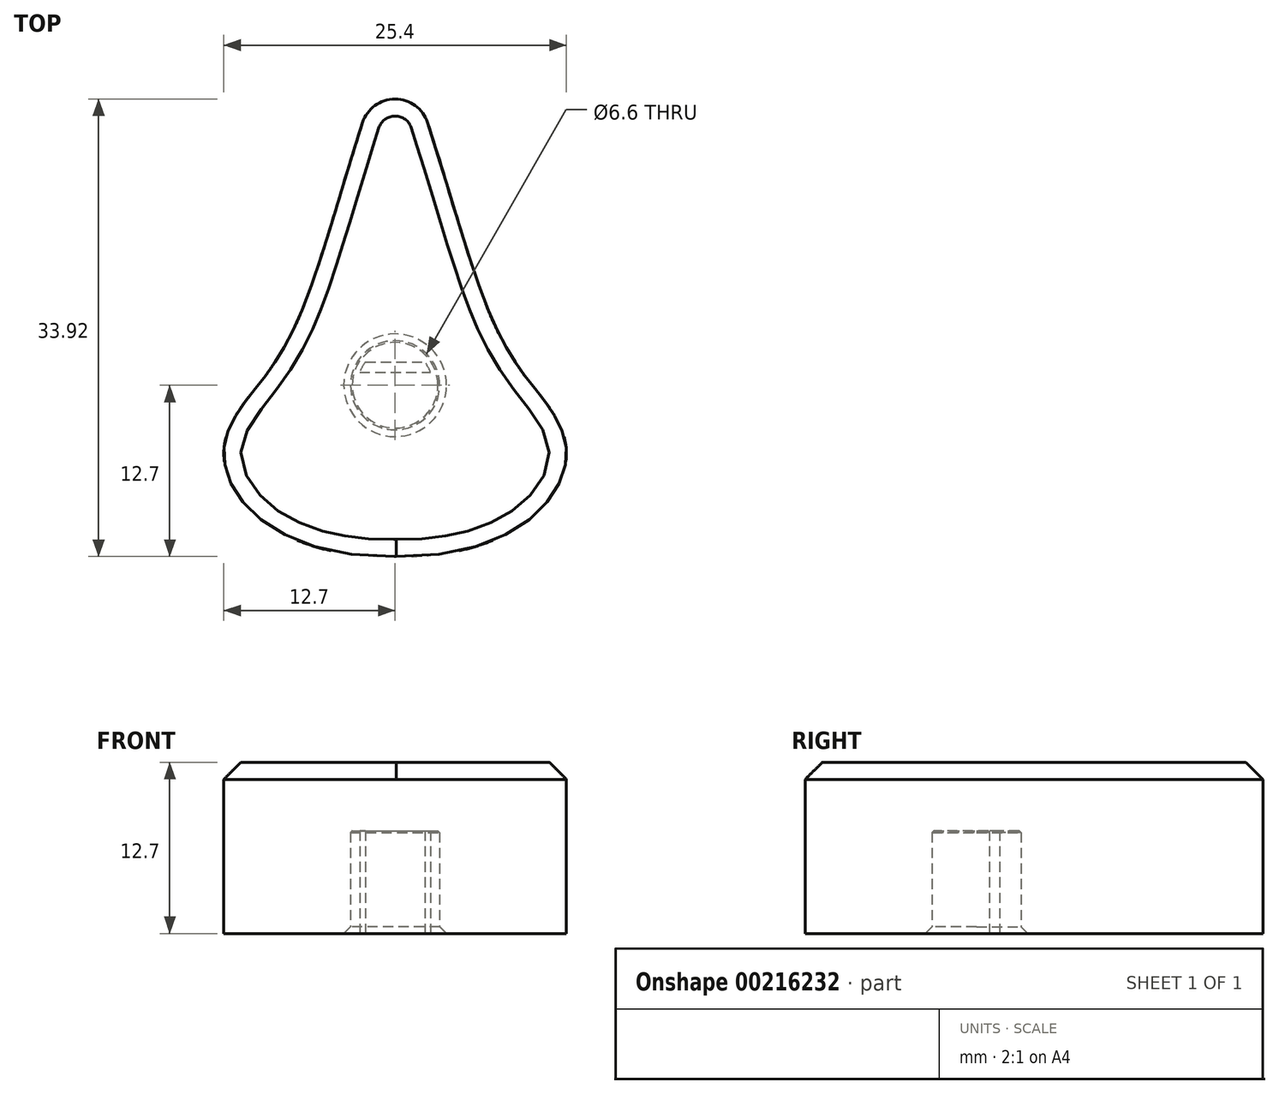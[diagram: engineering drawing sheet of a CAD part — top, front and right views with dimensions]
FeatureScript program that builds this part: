
annotation { "Feature Type Name" : "Feature", "Feature Type Description" : "" }
export const myFeature = defineFeature(function(context is Context, id is Id, definition is map)
    precondition{}
    {
        {
            var Q0;
            Q0=qCreatedBy(makeId("Top.planeOp"),FACE);
            var sketch = newSketch(context, id + "F0", { "sketchPlane" : qUnion([Q0])});
            skLineSegment(sketch, "E0", {"start": v(0, -12.7) * mm, "end": v(0, 25.4) * mm});
            skLineSegment(sketch, "E1", {"start": v(11.05, 11.4) * mm, "end": v(36.75, 22.83) * mm, "construction": true});
            skLineSegment(sketch, "E2", {"start": v(0, 0) * mm, "end": v(39.26, 10.52) * mm, "construction": true});
            skFitSpline(sketch, "E3", {"points": [v(0, -12.7) * mm, v(12.7, -5.22) * mm, v(10.16, 0) * mm, v(6.35, 7) * mm, v(0, 25.4) * mm], "startDerivative": vector(91.13, -1.7) * mm, "endDerivative": vector(-16.33, 22.75) * mm});
            skSolve(sketch);
        }
        {
            var Q0;
            Q0 = qSketchRegion(id + "F0", true);
            var Q1;
            Q1=sQuery(id+"F0.wireOp",EDGE,"c0f845b1-1718-4f25-a888-cf66eb396242");
            var Q2;
            Q2 = qBodyType(qCreatedBy(id + "F0" ,EDGE), BodyType.WIRE);
            extrude(context, id + "F1", {"entities" : qUnion([Q0]), "surfaceEntities" : qUnion([Q1, Q2]), "depth" : 12.7 * mm});
        }
        {
            var Q0;
            Q0=makeQuery(id+"F1.opExtrude","CAP_FACE",FACE,{"disambiguationData":[OSD([sQuery(id+"F0.wireOp",EDGE,"c0f845b1-1718-4f25-a888-cf66eb396242"),sQuery(id+"F0.wireOp",EDGE,"E0"),sQuery(id+"F0.wireOp",EDGE,"xmrPsXAH-aPoe-NY2f-SWT3-2pPE1XgSHqMv"),sQuery(id+"F0.wireOp",EDGE,"d0d9b82e-bfe0-46f1-ab0d-f52c297f3923"),sQuery(id+"F0.wireOp",EDGE,"4c88e3ce-19b1-495e-af78-50e4d5df14d2.trimOffspring"),sQuery(id+"F0.wireOp",EDGE,"cfbaa51a-1185-4897-8cd4-dc17d72ad261")])],"isStart":true});
            var sketch = newSketch(context, id + "F2", { "sketchPlane" : qUnion([Q0])});
            skArc(sketch, "E4", {"start": v(0, -3.3) * mm, "mid": v(3.3, 0) * mm, "end": v(0, 3.3) * mm});
            skLineSegment(sketch, "E5", {"start": v(0, -3.3) * mm, "end": v(0, -1.72) * mm});
            skLineSegment(sketch, "E6", {"start": v(0, 3.3) * mm, "end": v(-9.44, 3.3) * mm, "construction": true});
            skLineSegment(sketch, "E7", {"start": v(0, -0.96) * mm, "end": v(2.62, -0.96) * mm});
            skLineSegment(sketch, "E8", {"start": v(0, -1.72) * mm, "end": v(2.2, -1.72) * mm});
            skArc(sketch, "E9", {"start": v(2.2, -1.72) * mm, "mid": v(2.44, -1.36) * mm, "end": v(2.62, -0.96) * mm});
            skLineSegment(sketch, "E10.trimOffspring", {"start": v(0, -0.96) * mm, "end": v(0, 3.3) * mm});
            skSolve(sketch);
        }
        {
            var Q0;
            Q0 = qSketchRegion(id + "F2", true);
            extrude(context, id + "F3", {"entities" : qUnion([Q0]), "operationType" : NewBodyOperationType.REMOVE, "oppositeDirection" : true, "depth" : 7.62 * mm});
        }
        {
            var Q0;
            Q0=makeQuery(id+"F3.boolean.opBoolean","COPY",EDGE,{"derivedFrom":makeQuery(id+"F3.opExtrude","CAP_EDGE",EDGE,{"disambiguationData":[OSD([sQuery(id+"F2.wireOp",EDGE,"E4")])],"isStart":true})});
            chamfer(context, id + "F4", {"entities" : qUnion([Q0]), "width" : 0.5 * mm, "tangentPropagation" : true});
        }
        {
            var Q0;
            Q0=makeQuery(id+"F3.boolean.opBoolean","COPY",EDGE,{"derivedFrom":makeQuery(id+"F3.opExtrude","CAP_EDGE",EDGE,{"disambiguationData":[OSD([sQuery(id+"F2.wireOp",EDGE,"E4")])],"isStart":false})});
            chamfer(context, id + "F5", {"entities" : qUnion([Q0]), "width" : 0.13 * mm, "tangentPropagation" : true});
        }
        {
            var Q0;
            Q0=makeQuery(id+"F1.opExtrude","SWEPT_BODY",BODY,{"disambiguationData":[OSD([sQuery(id+"F0.wireOp",EDGE,"c0f845b1-1718-4f25-a888-cf66eb396242"),sQuery(id+"F0.wireOp",EDGE,"E0"),sQuery(id+"F0.wireOp",EDGE,"xmrPsXAH-aPoe-NY2f-SWT3-2pPE1XgSHqMv"),sQuery(id+"F0.wireOp",EDGE,"d0d9b82e-bfe0-46f1-ab0d-f52c297f3923"),sQuery(id+"F0.wireOp",EDGE,"4c88e3ce-19b1-495e-af78-50e4d5df14d2.trimOffspring"),sQuery(id+"F0.wireOp",EDGE,"cfbaa51a-1185-4897-8cd4-dc17d72ad261")])]});
            var Q1;
            Q1=qCreatedBy(makeId("Right.planeOp"),FACE);
            mirror(context, id + "F6", {"operationType" : NewBodyOperationType.ADD, "entities" : qUnion([Q0]), "mirrorPlane" : qUnion([Q1])});
        }
        {
            var Q0;
            {var subQ0=sQuery(id+"F0.wireOp",EDGE,"E3");var subQ1=sQuery(id+"F0.wireOp",EDGE,"E0");var subQ2=makeQuery(id+"F1.opExtrude","SWEPT_EDGE",EDGE,{"disambiguationData":[OSD([subQ1,subQ0]),TDD([makeQuery(id+"F0.imprint","INTERSECT",VERTEX,{"disambiguationData":[OD(0.0)],"derivedFrom":[subQ1,subQ0]})])]});Q0=makeQuery(id+"F6.boolean.opBoolean","MERGE",EDGE,{"derivedFrom":[subQ2,makeQuery(id+"F6.opPattern","COPY",EDGE,{"derivedFrom":subQ2,"instanceName":"1"})]});}
            fillet(context, id + "F7", {"entities" : qUnion([Q0]), "radius" : 5.08 * mm, "rho" : 0.5, "crossSection" : FilletCrossSection.CONIC, "allowEdgeOverflow" : false});
        }
        {
            var Q0;
            {var subQ0=sQuery(id+"F0.wireOp",EDGE,"E3");var subQ1=sQuery(id+"F0.wireOp",EDGE,"E0");var subQ2=makeQuery(id+"F1.opExtrude","SWEPT_EDGE",EDGE,{"disambiguationData":[OSD([subQ1,subQ0]),TDD([makeQuery(id+"F0.imprint","INTERSECT",VERTEX,{"disambiguationData":[OD(1.0)],"derivedFrom":[subQ1,subQ0]})])]});Q0=makeQuery(id+"F6.boolean.opBoolean","MERGE",EDGE,{"derivedFrom":[subQ2,makeQuery(id+"F6.opPattern","COPY",EDGE,{"derivedFrom":subQ2,"instanceName":"1"})]});}
            fillet(context, id + "F8", {"entities" : qUnion([Q0]), "radius" : 2.54 * mm, "tangentPropagation" : true, "allowEdgeOverflow" : false});
        }
        {
            var Q0;
            Q0=makeQuery(id+"F1.opExtrude","CAP_EDGE",EDGE,{"disambiguationData":[OSD([sQuery(id+"F0.wireOp",EDGE,"E3")])],"isStart":false});
            chamfer(context, id + "F9", {"entities" : qUnion([Q0]), "width" : 1.27 * mm, "tangentPropagation" : true});
        }
    });
